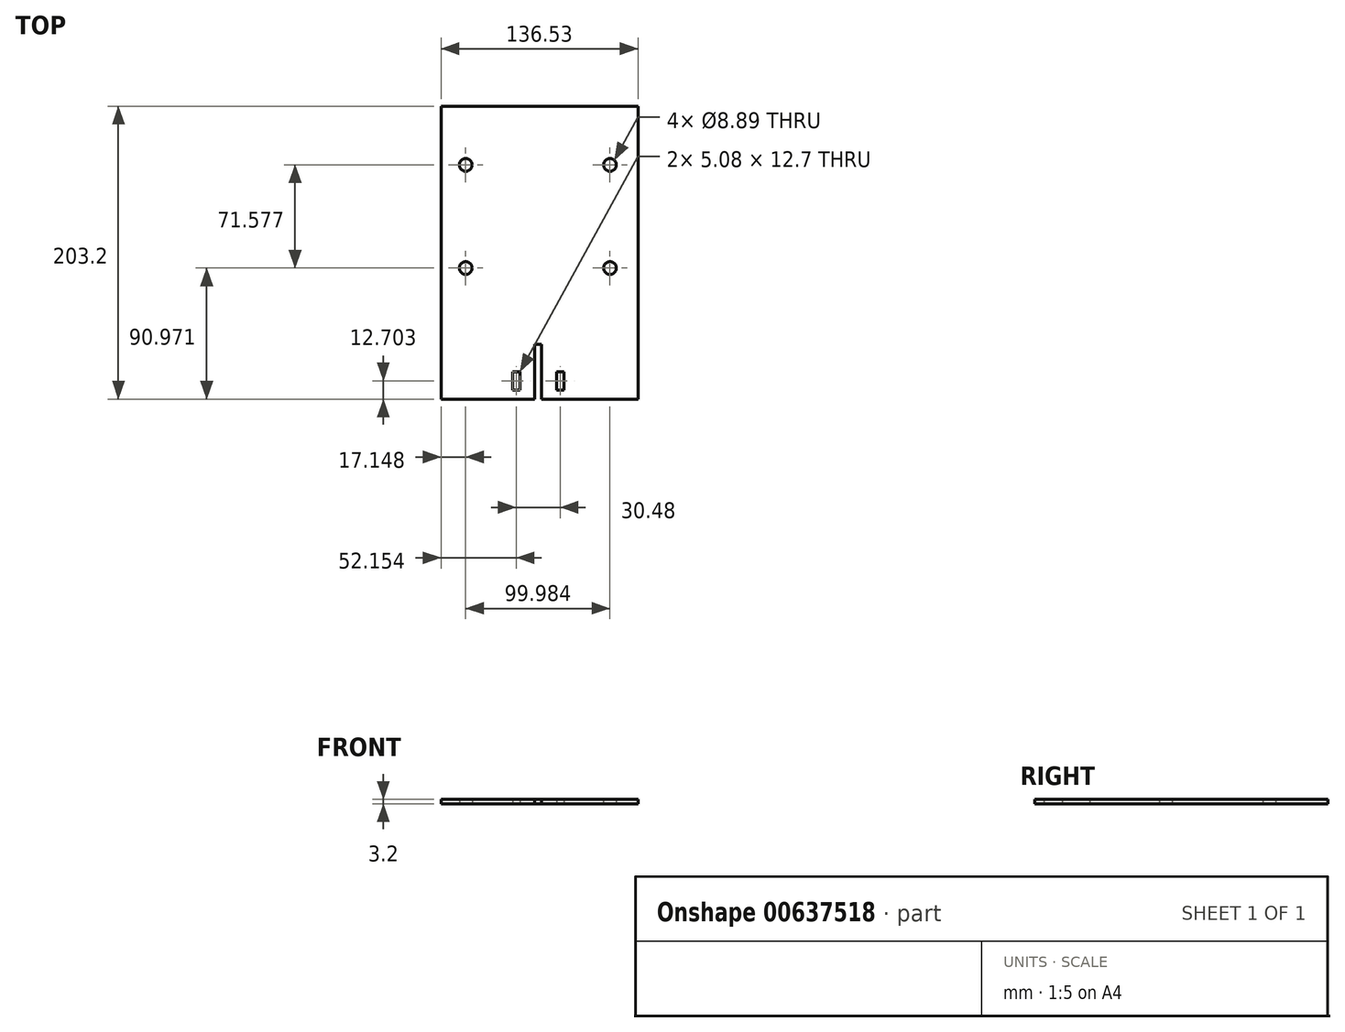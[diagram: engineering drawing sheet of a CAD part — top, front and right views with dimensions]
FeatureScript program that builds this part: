
annotation { "Feature Type Name" : "Feature", "Feature Type Description" : "" }
export const myFeature = defineFeature(function(context is Context, id is Id, definition is map)
    precondition{}
    {
        {
            var Q0;
            Q0=qCreatedBy(makeId("Top.planeOp"),FACE);
            var sketch = newSketch(context, id + "F0", { "sketchPlane" : qUnion([Q0])});
            skLineSegment(sketch, "E0.bottom", {"start": v(-67.14, 76.44) * mm, "end": v(69.39, 76.44) * mm});
            skLineSegment(sketch, "E0.top", {"start": v(-67.14, -126.76) * mm, "end": v(69.39, -126.76) * mm});
            skLineSegment(sketch, "E0.left", {"start": v(-67.14, 76.44) * mm, "end": v(-67.14, -126.76) * mm});
            skLineSegment(sketch, "E0.right", {"start": v(69.39, 76.44) * mm, "end": v(69.39, -126.76) * mm});
            skLineSegment(sketch, "E1.1", {"start": v(-67.14, -126.76) * mm, "end": v(-67.14, 76.44) * mm, "construction": true});
            skLineSegment(sketch, "E1.8", {"start": v(-67.14, -126.76) * mm, "end": v(69.39, -126.76) * mm, "construction": true});
            skLineSegment(sketch, "E2.bottom", {"start": v(18.03, -120.4) * mm, "end": v(12.95, -120.4) * mm});
            skLineSegment(sketch, "E2.top", {"start": v(18.03, -107.7) * mm, "end": v(12.95, -107.7) * mm});
            skLineSegment(sketch, "E2.left", {"start": v(18.03, -120.4) * mm, "end": v(18.03, -107.7) * mm});
            skLineSegment(sketch, "E2.right", {"start": v(12.95, -120.4) * mm, "end": v(12.95, -107.7) * mm});
            skPoint(sketch, "E2.middle", {"position": v(15.5, -114.06) * mm});
            skLineSegment(sketch, "E3.MirrorCS", {"start": v(-17.53, -107.7) * mm, "end": v(-12.45, -107.7) * mm});
            skLineSegment(sketch, "E4.MirrorCS", {"start": v(-12.45, -120.4) * mm, "end": v(-12.45, -107.7) * mm});
            skLineSegment(sketch, "E5.MirrorCS", {"start": v(-17.53, -120.4) * mm, "end": v(-17.53, -107.7) * mm});
            skLineSegment(sketch, "E6.MirrorCS", {"start": v(-17.53, -120.4) * mm, "end": v(-12.45, -120.4) * mm});
            skLineSegment(sketch, "E7.bottom", {"start": v(-2.2, -88.66) * mm, "end": v(2.72, -88.66) * mm});
            skLineSegment(sketch, "E7.top", {"start": v(-2.2, -126.76) * mm, "end": v(2.72, -126.76) * mm});
            skLineSegment(sketch, "E7.left", {"start": v(-2.2, -88.66) * mm, "end": v(-2.2, -126.76) * mm});
            skLineSegment(sketch, "E7.right", {"start": v(2.72, -88.66) * mm, "end": v(2.72, -126.76) * mm});
            skPoint(sketch, "E7.middle", {"position": v(0.25, -107.7) * mm});
            skCircle(sketch, "E8", {"center": v(-50, 35.79) * mm, "radius": 4.45 * mm});
            skCircle(sketch, "E9.MirrorC", {"center": v(-50, -35.79) * mm, "radius": 4.45 * mm});
            skCircle(sketch, "E10.MirrorC", {"center": v(50, 35.79) * mm, "radius": 4.45 * mm});
            skCircle(sketch, "E11.MirrorC", {"center": v(50, -35.79) * mm, "radius": 4.45 * mm});
            skSolve(sketch);
        }
        {
            var Q0;
            Q0=makeQuery(id+"F0.imprint","IMPRINT",FACE,{"disambiguationData":[TD([[makeQuery(id+"F0.imprint","IMPRINT",EDGE,{"derivedFrom":sQuery(id+"F0.wireOp",EDGE,"E0.bottom")}),-1.0]])]});
            extrude(context, id + "F1", {"entities" : qUnion([Q0]), "depth" : 3.2 * mm, "offsetDistance" : 25.4 * mm});
        }
    });
